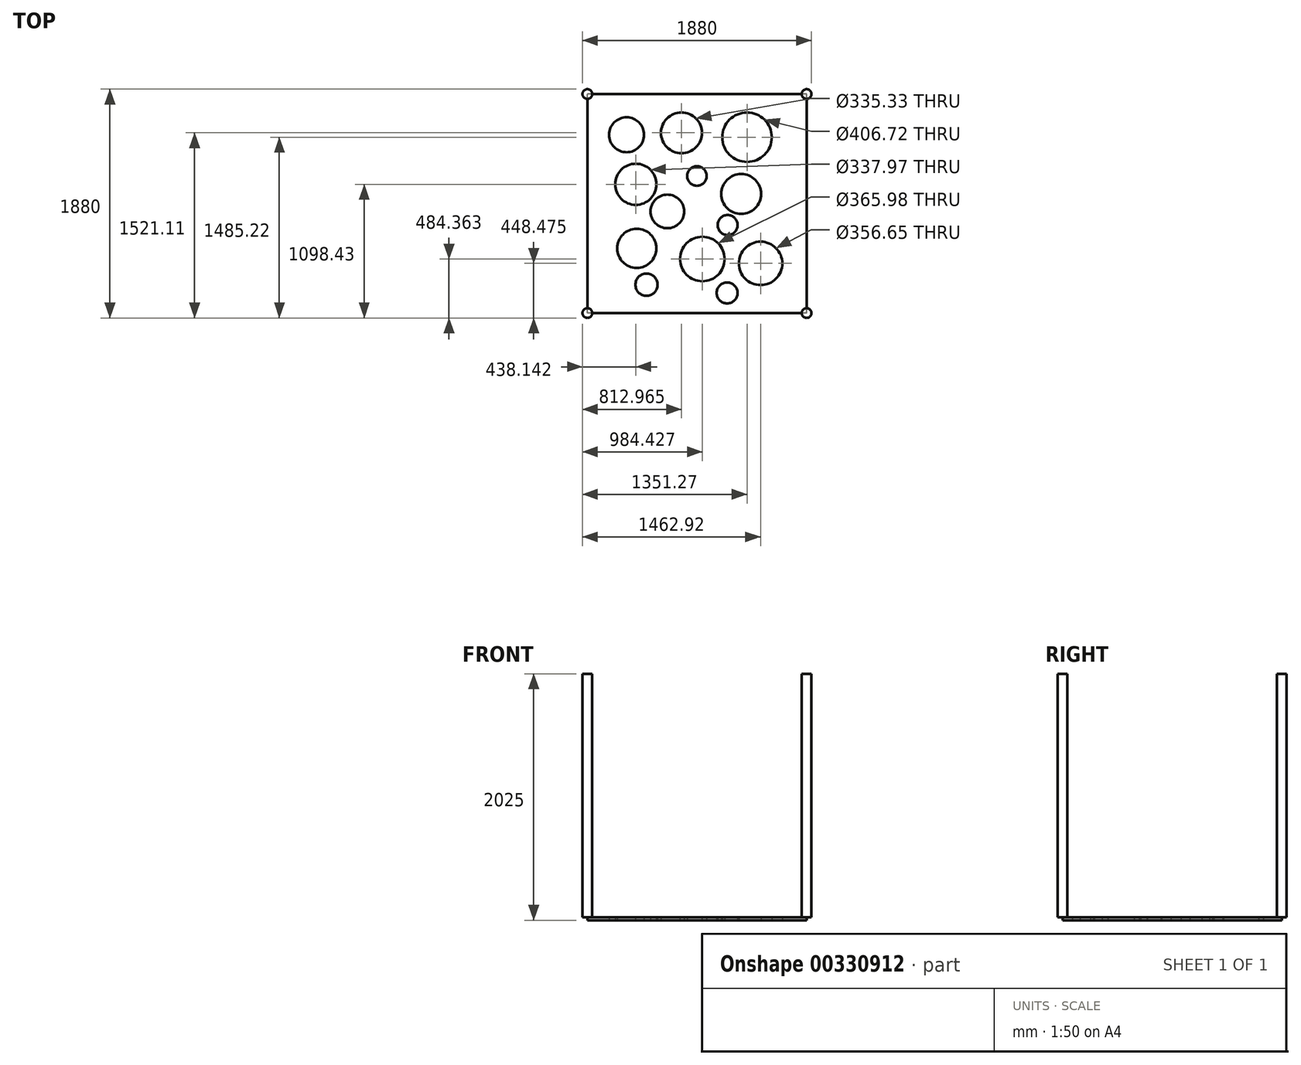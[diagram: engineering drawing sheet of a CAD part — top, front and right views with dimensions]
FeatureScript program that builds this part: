
annotation { "Feature Type Name" : "Feature", "Feature Type Description" : "" }
export const myFeature = defineFeature(function(context is Context, id is Id, definition is map)
    precondition{}
    {
        {
            var Q0;
            Q0=qCreatedBy(makeId("Top.planeOp"),FACE);
            var sketch = newSketch(context, id + "F0", { "sketchPlane" : qUnion([Q0])});
            skLineSegment(sketch, "E0.bottom", {"start": v(900, -900) * mm, "end": v(-900, -900) * mm});
            skLineSegment(sketch, "E0.top", {"start": v(900, 900) * mm, "end": v(-900, 900) * mm});
            skLineSegment(sketch, "E0.left", {"start": v(900, -900) * mm, "end": v(900, 900) * mm});
            skLineSegment(sketch, "E0.right", {"start": v(-900, -900) * mm, "end": v(-900, 900) * mm});
            skPoint(sketch, "E0.middle", {"position": v(0, 0) * mm});
            skCircle(sketch, "E1", {"center": v(-577.62, 565.16) * mm, "radius": 143.6 * mm});
            skCircle(sketch, "E2", {"center": v(-127.04, 581.1) * mm, "radius": 167.66 * mm});
            skCircle(sketch, "E3", {"center": v(411.27, 545.22) * mm, "radius": 203.36 * mm});
            skCircle(sketch, "E4", {"center": v(-501.86, 158.43) * mm, "radius": 168.99 * mm});
            skCircle(sketch, "E5", {"center": v(363.42, 78.68) * mm, "radius": 164.26 * mm});
            skCircle(sketch, "E6", {"center": v(-493.88, -367.91) * mm, "radius": 160.54 * mm});
            skCircle(sketch, "E7", {"center": v(44.43, -455.64) * mm, "radius": 183 * mm});
            skCircle(sketch, "E8", {"center": v(522.92, -491.52) * mm, "radius": 178.33 * mm});
            skCircle(sketch, "E9", {"center": v(-414.13, -666.97) * mm, "radius": 91.02 * mm});
            skCircle(sketch, "E10", {"center": v(-242.67, -64.86) * mm, "radius": 138.18 * mm});
            skCircle(sketch, "E11", {"center": v(0, 226.22) * mm, "radius": 80.2 * mm});
            skCircle(sketch, "E12", {"center": v(251.78, -176.51) * mm, "radius": 82.2 * mm});
            skCircle(sketch, "E13", {"center": v(247.79, -734.76) * mm, "radius": 85.9 * mm});
            skSolve(sketch);
        }
        {
            var Q0;
            Q0=makeQuery(id+"F0.imprint","IMPRINT",FACE,{"disambiguationData":[TD([[makeQuery(id+"F0.imprint","IMPRINT",EDGE,{"derivedFrom":sQuery(id+"F0.wireOp",EDGE,"E0.bottom")}),-1.0]])]});
            extrude(context, id + "F1", {"entities" : qUnion([Q0]), "depth" : 25 * mm});
        }
        {
            var Q0;
            Q0=makeQuery(id+"F1.opExtrude","CAP_FACE",FACE,{"disambiguationData":[OSD([sQuery(id+"F0.wireOp",EDGE,"E0.bottom"),sQuery(id+"F0.wireOp",EDGE,"E0.top"),sQuery(id+"F0.wireOp",EDGE,"E0.left"),sQuery(id+"F0.wireOp",EDGE,"E0.right"),sQuery(id+"F0.wireOp",EDGE,"E1"),sQuery(id+"F0.wireOp",EDGE,"E2"),sQuery(id+"F0.wireOp",EDGE,"E3"),sQuery(id+"F0.wireOp",EDGE,"E4"),sQuery(id+"F0.wireOp",EDGE,"E5"),sQuery(id+"F0.wireOp",EDGE,"E6"),sQuery(id+"F0.wireOp",EDGE,"E7"),sQuery(id+"F0.wireOp",EDGE,"E8"),sQuery(id+"F0.wireOp",EDGE,"E9"),sQuery(id+"F0.wireOp",EDGE,"E10"),sQuery(id+"F0.wireOp",EDGE,"E11"),sQuery(id+"F0.wireOp",EDGE,"E12"),sQuery(id+"F0.wireOp",EDGE,"E13")])],"isStart":false});
            var sketch = newSketch(context, id + "F2", { "sketchPlane" : qUnion([Q0])});
            skCircle(sketch, "E14", {"center": v(900, 900) * mm, "radius": 40 * mm});
            skCircle(sketch, "E15", {"center": v(900, -900) * mm, "radius": 40 * mm});
            skCircle(sketch, "E16", {"center": v(-900, 900) * mm, "radius": 40 * mm});
            skCircle(sketch, "E17", {"center": v(-900, -900) * mm, "radius": 40 * mm});
            skSolve(sketch);
        }
        {
            var Q0;
            Q0 = qSketchRegion(id + "F2", true);
            extrude(context, id + "F3", {"entities" : qUnion([Q0]), "operationType" : NewBodyOperationType.ADD, "depth" : 2000 * mm});
        }
    });
